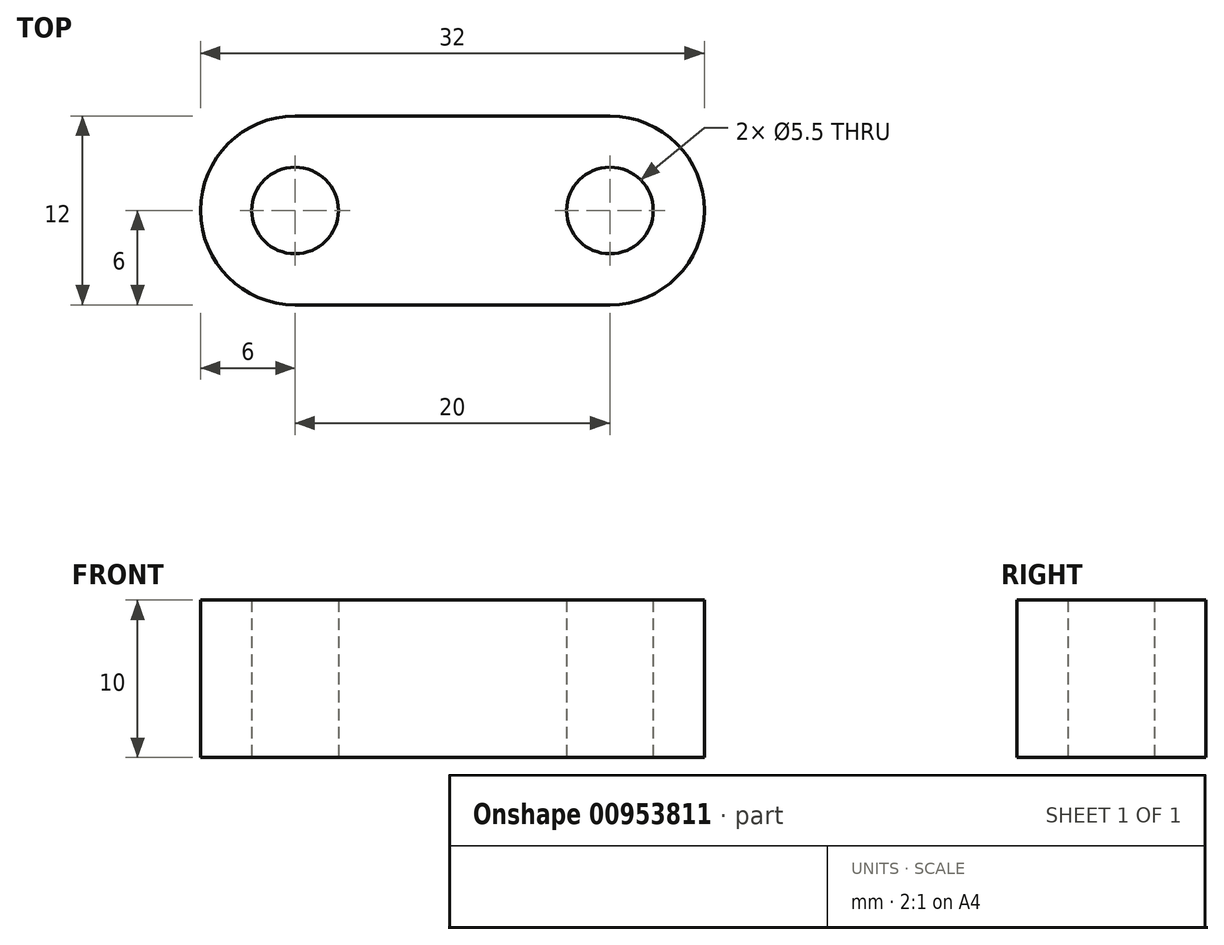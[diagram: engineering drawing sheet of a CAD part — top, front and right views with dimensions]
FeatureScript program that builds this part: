
annotation { "Feature Type Name" : "Feature", "Feature Type Description" : "" }
export const myFeature = defineFeature(function(context is Context, id is Id, definition is map)
    precondition{}
    {
        {
            var Q0;
            Q0=qCreatedBy(makeId("Top.planeOp"),FACE);
            var sketch = newSketch(context, id + "F0", { "sketchPlane" : qUnion([Q0])});
            skCircle(sketch, "E0", {"center": v(0, 0) * mm, "radius": 2.75 * mm});
            skCircle(sketch, "E1", {"center": v(20, 0) * mm, "radius": 2.75 * mm});
            skLineSegment(sketch, "E2.bottom", {"start": v(-6, 6) * mm, "end": v(26, 6) * mm});
            skLineSegment(sketch, "E2.top", {"start": v(-6, -6) * mm, "end": v(26, -6) * mm});
            skLineSegment(sketch, "E2.left", {"start": v(-6, 6) * mm, "end": v(-6, -6) * mm});
            skLineSegment(sketch, "E2.right", {"start": v(26, 6) * mm, "end": v(26, -6) * mm});
            skSolve(sketch);
        }
        {
            var Q0;
            Q0=makeQuery(id+"F0.imprint","IMPRINT",FACE,{"disambiguationData":[TD([[makeQuery(id+"F0.imprint","IMPRINT",EDGE,{"derivedFrom":sQuery(id+"F0.wireOp",EDGE,"E0")}),-1.0]])]});
            extrude(context, id + "F1", {"entities" : qUnion([Q0]), "depth" : 10 * mm, "offsetDistance" : 25 * mm});
        }
        {
            var Q0;
            Q0=makeQuery(id+"F1.opExtrude","SWEPT_EDGE",EDGE,{"disambiguationData":[OSD([sQuery(id+"F0.wireOp",EDGE,"E2.top"),sQuery(id+"F0.wireOp",EDGE,"E2.left")])]});
            var Q1;
            Q1=makeQuery(id+"F1.opExtrude","SWEPT_EDGE",EDGE,{"disambiguationData":[OSD([sQuery(id+"F0.wireOp",EDGE,"E2.bottom"),sQuery(id+"F0.wireOp",EDGE,"E2.left")])]});
            var Q2;
            Q2=makeQuery(id+"F1.opExtrude","SWEPT_EDGE",EDGE,{"disambiguationData":[OSD([sQuery(id+"F0.wireOp",EDGE,"E2.top"),sQuery(id+"F0.wireOp",EDGE,"E2.right")])]});
            var Q3;
            Q3=makeQuery(id+"F1.opExtrude","SWEPT_EDGE",EDGE,{"disambiguationData":[OSD([sQuery(id+"F0.wireOp",EDGE,"E2.bottom"),sQuery(id+"F0.wireOp",EDGE,"E2.right")])]});
            fillet(context, id + "F2", {"entities" : qUnion([Q0, Q1, Q2, Q3]), "radius" : 6 * mm, "tangentPropagation" : true, "allowEdgeOverflow" : false});
        }
    });
